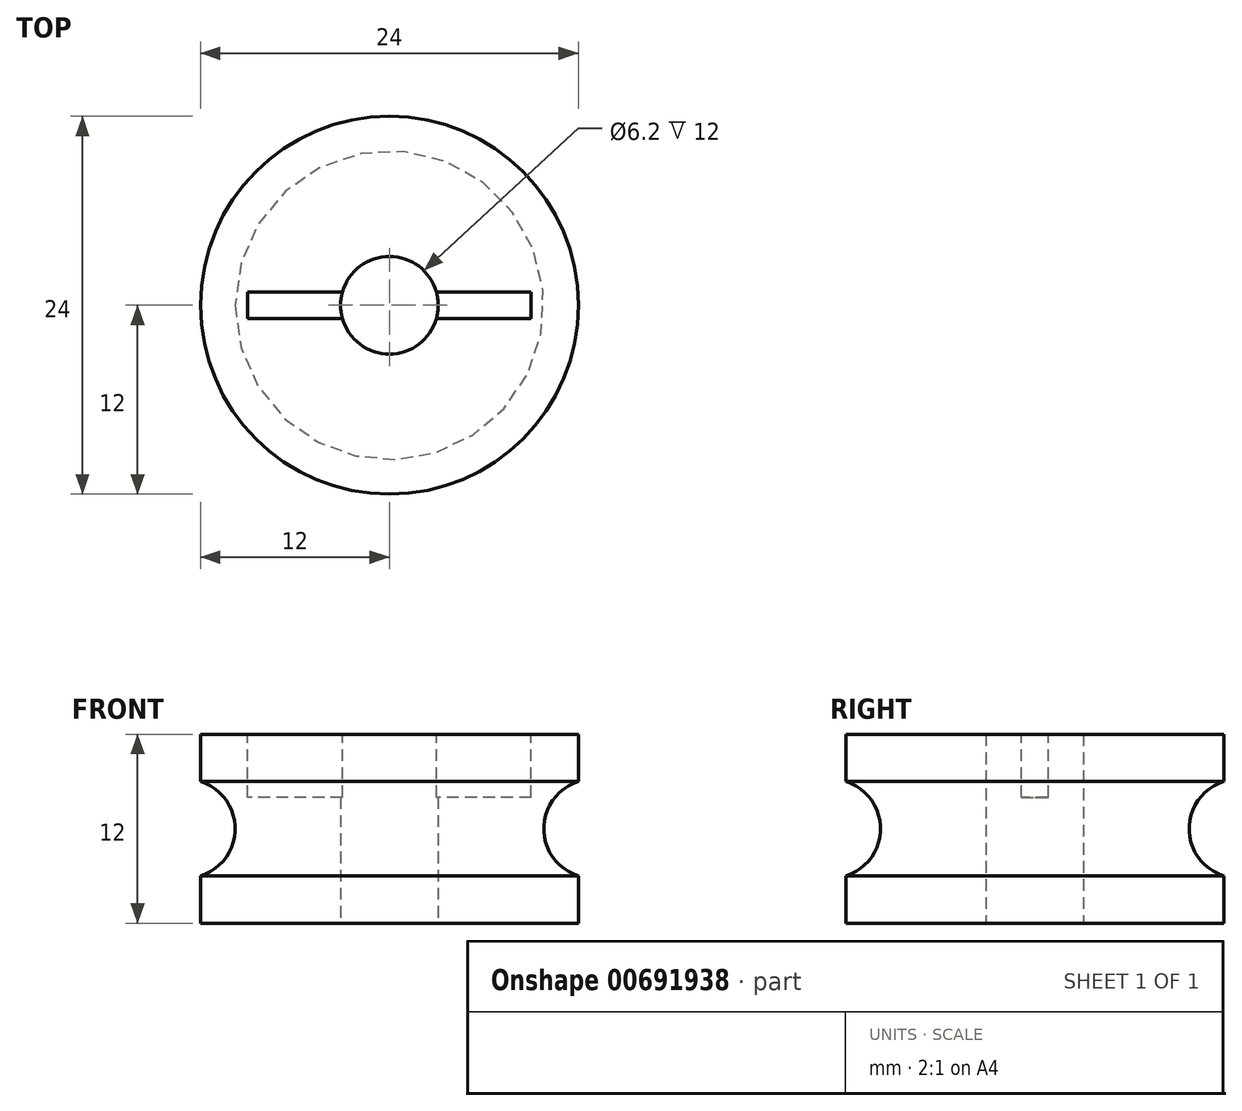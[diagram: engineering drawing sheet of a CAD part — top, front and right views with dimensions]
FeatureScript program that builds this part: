
annotation { "Feature Type Name" : "Feature", "Feature Type Description" : "" }
export const myFeature = defineFeature(function(context is Context, id is Id, definition is map)
    precondition{}
    {
        {
            var Q0;
            Q0=qCreatedBy(makeId("Front.planeOp"),FACE);
            var sketch = newSketch(context, id + "F0", { "sketchPlane" : qUnion([Q0])});
            skLineSegment(sketch, "E0", {"start": v(12, 12) * mm, "end": v(12, 9) * mm});
            skLineSegment(sketch, "E1", {"start": v(12, 3) * mm, "end": v(12, 0) * mm});
            skLineSegment(sketch, "E2", {"start": v(12, 0) * mm, "end": v(3.1, 0) * mm});
            skLineSegment(sketch, "E3", {"start": v(3.1, 0) * mm, "end": v(3.1, 12) * mm});
            skLineSegment(sketch, "E4", {"start": v(3.1, 12) * mm, "end": v(12, 12) * mm});
            skArc(sketch, "E5", {"start": v(12, 9) * mm, "mid": v(9.8, 6) * mm, "end": v(12, 3) * mm});
            skLineSegment(sketch, "E6", {"start": v(0, 0) * mm, "end": v(0, 16.95) * mm});
            skSolve(sketch);
        }
        {
            var Q0;
            Q0=makeQuery(id+"F0.imprint","IMPRINT",FACE,{"disambiguationData":[TD([[makeQuery(id+"F0.imprint","IMPRINT",EDGE,{"derivedFrom":sQuery(id+"F0.wireOp",EDGE,"E0")}),-1.0]])]});
            var Q1;
            Q1=sQuery(id+"F0.wireOp",EDGE,"E6");
            revolve(context, id + "F1", {"surfaceOperationType" : NewSurfaceOperationType.NEW, "entities" : qUnion([Q0]), "axis" : qUnion([Q1]), "revolveType" : RevolveType.FULL});
        }
        {
            var Q0;
            Q0=makeQuery(id+"F1.opRevolve","SWEPT_FACE",FACE,{"disambiguationData":[OSD([sQuery(id+"F0.wireOp",EDGE,"E4")])]});
            var sketch = newSketch(context, id + "F2", { "sketchPlane" : qUnion([Q0])});
            skLineSegment(sketch, "E7.bottom", {"start": v(9, -0.85) * mm, "end": v(-9, -0.85) * mm});
            skLineSegment(sketch, "E7.top", {"start": v(9, 0.85) * mm, "end": v(-9, 0.85) * mm});
            skLineSegment(sketch, "E7.left", {"start": v(9, -0.85) * mm, "end": v(9, 0.85) * mm});
            skLineSegment(sketch, "E7.right", {"start": v(-9, -0.85) * mm, "end": v(-9, 0.85) * mm});
            skPoint(sketch, "E7.middle", {"position": v(0, 0) * mm});
            skSolve(sketch);
        }
        {
            var Q0;
            {var subQ0=sQuery(id+"F2.wireOp",EDGE,"E7.right");Q0=makeQuery(id+"F2.imprint","IMPRINT",FACE,{"disambiguationData":[TD([[makeQuery(id+"F2.imprint","IMPRINT",EDGE,{"derivedFrom":subQ0}),-1.0]])]});}
            var Q1;
            {var subQ0=sQuery(id+"F2.wireOp",EDGE,"E7.left");Q1=makeQuery(id+"F2.imprint","IMPRINT",FACE,{"disambiguationData":[TD([[makeQuery(id+"F2.imprint","IMPRINT",EDGE,{"derivedFrom":subQ0}),1.0]])]});}
            extrude(context, id + "F3", {"entities" : qUnion([Q0, Q1]), "operationType" : NewBodyOperationType.REMOVE, "oppositeDirection" : true, "depth" : 4 * mm, "offsetDistance" : 25 * mm});
        }
    });
